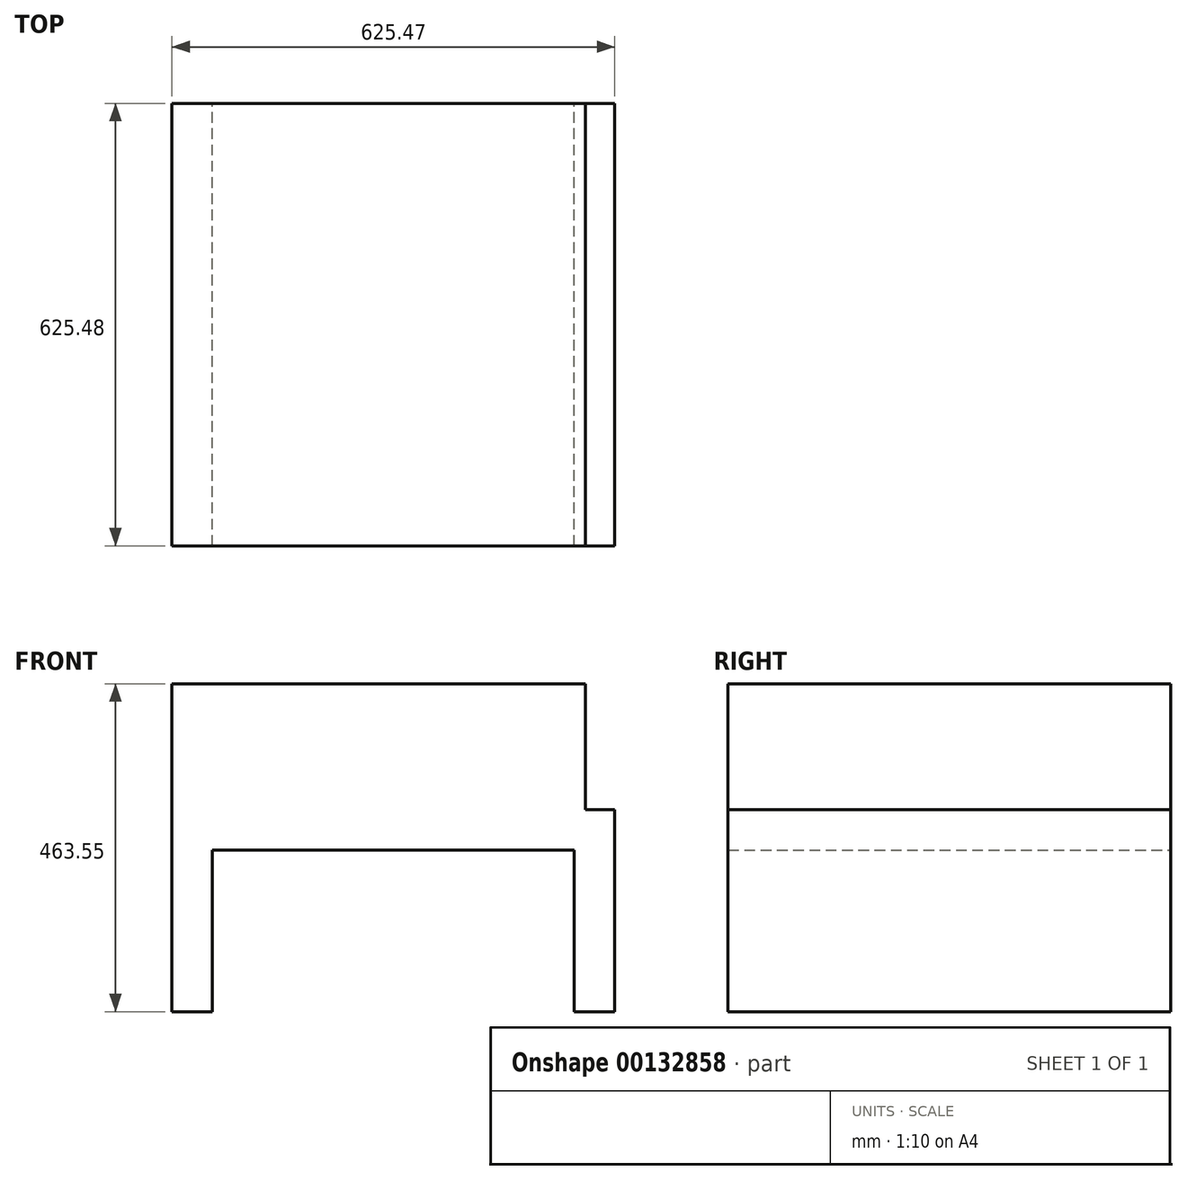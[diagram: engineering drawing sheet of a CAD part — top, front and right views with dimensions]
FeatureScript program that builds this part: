
annotation { "Feature Type Name" : "Feature", "Feature Type Description" : "" }
export const myFeature = defineFeature(function(context is Context, id is Id, definition is map)
    precondition{}
    {
        {
            var Q0;
            Q0=qCreatedBy(makeId("Front.planeOp"),FACE);
            var sketch = newSketch(context, id + "F0", { "sketchPlane" : qUnion([Q0])});
            skLineSegment(sketch, "E0", {"start": v(-140.62, 0) * mm, "end": v(484.85, 0) * mm});
            skLineSegment(sketch, "E1", {"start": v(484.85, 0) * mm, "end": v(484.85, -285.75) * mm});
            skLineSegment(sketch, "E2", {"start": v(484.85, -285.75) * mm, "end": v(427.7, -285.75) * mm});
            skLineSegment(sketch, "E3", {"start": v(427.7, -285.75) * mm, "end": v(427.7, -57.15) * mm});
            skLineSegment(sketch, "E4", {"start": v(427.7, -57.15) * mm, "end": v(-83.47, -57.15) * mm});
            skLineSegment(sketch, "E5", {"start": v(-83.47, -57.15) * mm, "end": v(-83.47, -285.75) * mm});
            skLineSegment(sketch, "E6", {"start": v(-83.47, -285.75) * mm, "end": v(-140.62, -285.75) * mm});
            skLineSegment(sketch, "E7", {"start": v(-140.62, -285.75) * mm, "end": v(-140.62, 0) * mm});
            skLineSegment(sketch, "E8", {"start": v(-140.62, 0) * mm, "end": v(-140.62, 177.8) * mm});
            skLineSegment(sketch, "E9", {"start": v(-140.62, 177.8) * mm, "end": v(443.58, 177.8) * mm});
            skLineSegment(sketch, "E10", {"start": v(443.58, 177.8) * mm, "end": v(443.58, 0) * mm});
            skSolve(sketch);
        }
        {
            var Q0;
            Q0 = qSketchRegion(id + "F0", true);
            extrude(context, id + "F1", {"entities" : qUnion([Q0]), "endBound" : BoundingType.SYMMETRIC, "depth" : 625.47 * mm});
        }
    });
